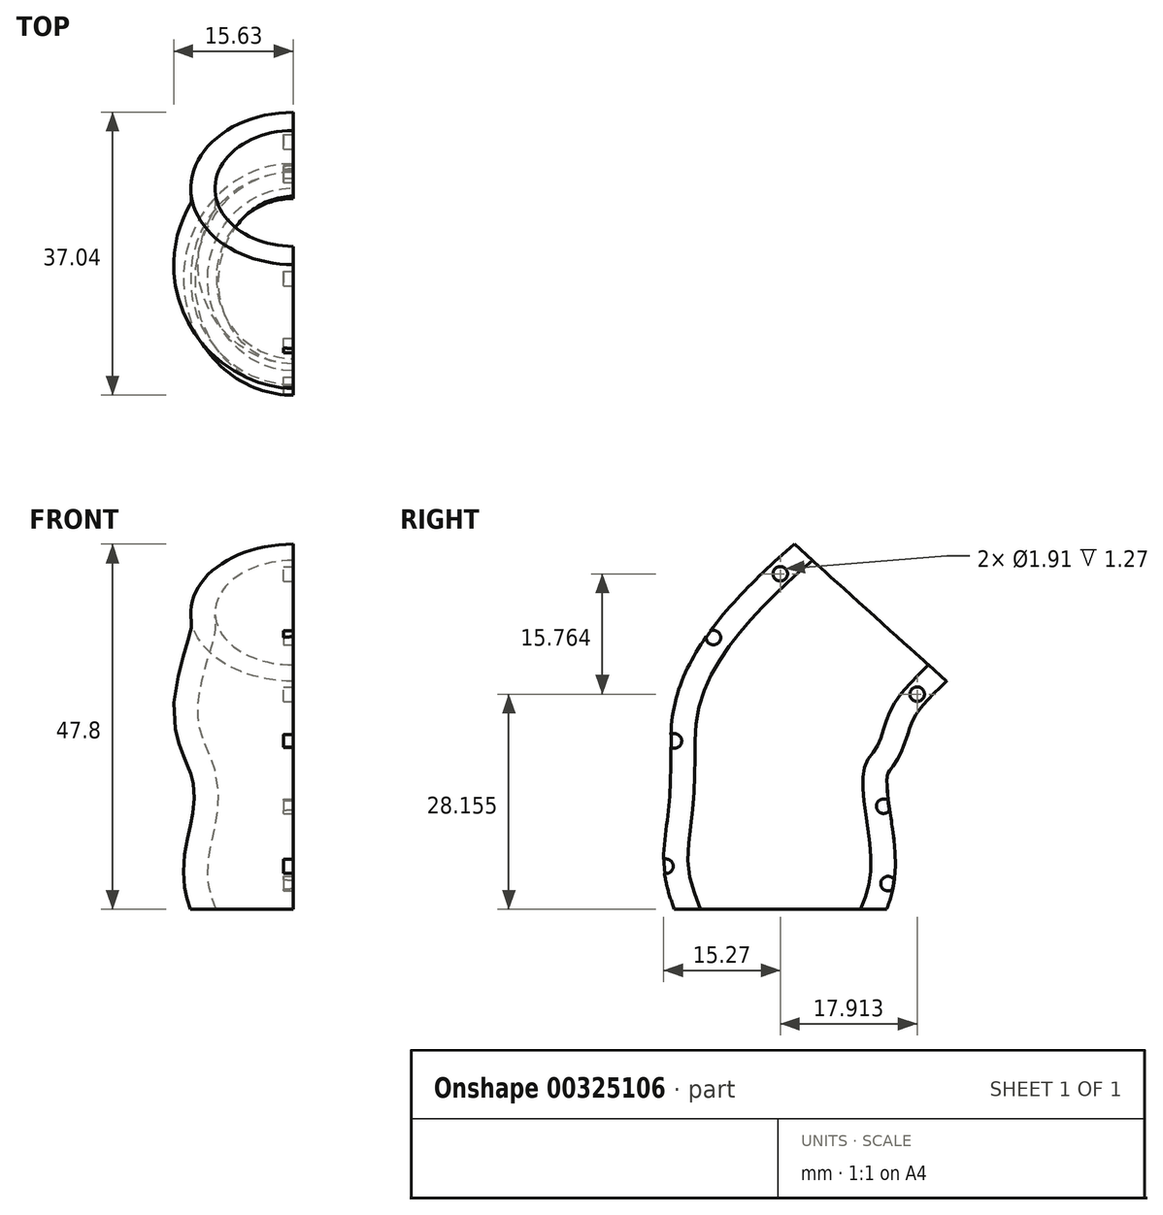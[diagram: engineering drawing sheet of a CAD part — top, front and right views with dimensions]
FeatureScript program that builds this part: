
annotation { "Feature Type Name" : "Feature", "Feature Type Description" : "" }
export const myFeature = defineFeature(function(context is Context, id is Id, definition is map)
    precondition{}
    {
        {
            var Q0;
            Q0=qCreatedBy(makeId("Top.planeOp"),FACE);
            var sketch = newSketch(context, id + "F0", { "sketchPlane" : qUnion([Q0])});
            skEllipse(sketch, "E0", {"center": v(0, 0) * mm, "majorRadius": 10.48 * mm, "minorRadius": 10.06 * mm, "majorAxis": v(0, 1)});
            skSolve(sketch);
        }
        {
            var Q0;
            Q0=qCreatedBy(makeId("Top.planeOp"),FACE);
            cPlane(context, id + "F1", {"entities" : qUnion([Q0]), "cplaneType" : CPlaneType.OFFSET, "offset" : 3.17 * mm, "width" : 152.4 * mm, "height" : 152.4 * mm});
        }
        {
            var Q0;
            Q0=qCreatedBy(id+"F1.planeOp",FACE);
            var sketch = newSketch(context, id + "F2", { "sketchPlane" : qUnion([Q0])});
            skEllipse(sketch, "E1", {"center": v(0, 0) * mm, "majorRadius": 11.6 * mm, "minorRadius": 11.04 * mm, "majorAxis": v(0, 1)});
            skSolve(sketch);
        }
        {
            var Q0;
            Q0=qCreatedBy(makeId("Top.planeOp"),FACE);
            cPlane(context, id + "F3", {"entities" : qUnion([Q0]), "cplaneType" : CPlaneType.OFFSET, "offset" : 19.05 * mm, "width" : 152.4 * mm, "height" : 152.4 * mm});
        }
        {
            var Q0;
            Q0=qCreatedBy(id+"F3.planeOp",FACE);
            var sketch = newSketch(context, id + "F4", { "sketchPlane" : qUnion([Q0])});
            skEllipse(sketch, "E2", {"center": v(0, 0) * mm, "majorRadius": 11.18 * mm, "minorRadius": 10.48 * mm, "majorAxis": v(0, -1)});
            skSolve(sketch);
        }
        {
            var Q0;
            Q0=qCreatedBy(makeId("Right.planeOp"),FACE);
            var sketch = newSketch(context, id + "F5", { "sketchPlane" : qUnion([Q0])});
            skLineSegment(sketch, "E3", {"start": v(-8.35, 25.4) * mm, "end": v(9.56, 21.59) * mm});
            skSolve(sketch);
        }
        {
            var Q0;
            Q0=qCreatedBy(makeId("Right.planeOp"),FACE);
            var Q1;
            Q1=qBodyType(qCreatedBy(id+"F5",EDGE),BodyType.WIRE);
            cPlane(context, id + "F6", {"entities" : qUnion([Q0, Q1]), "cplaneType" : CPlaneType.LINE_ANGLE, "offset" : 25.4 * mm, "angle" : 90 * degree, "width" : 152.4 * mm, "height" : 152.4 * mm});
        }
        {
            var Q0;
            Q0=qCreatedBy(id+"F6.planeOp",FACE);
            var sketch = newSketch(context, id + "F7", { "sketchPlane" : qUnion([Q0])});
            skEllipse(sketch, "E4", {"center": v(0, -4.06) * mm, "majorRadius": 11.87 * mm, "minorRadius": 12.15 * mm, "majorAxis": v(0, 1)});
            skSolve(sketch);
        }
        {
            var Q0;
            Q0=qCreatedBy(id+"F6.planeOp",FACE);
            var sketch = newSketch(context, id + "F8", { "sketchPlane" : qUnion([Q0])});
            skLineSegment(sketch, "E5", {"start": v(11.1, -4.63) * mm, "end": v(-10.76, -4.63) * mm});
            skSolve(sketch);
        }
        {
            var Q0;
            Q0=sQuery(id+"F8.wireOp",EDGE,"E5");
            var Q1;
            Q1=qCreatedBy(id+"F6.planeOp",FACE);
            cPlane(context, id + "F9", {"entities" : qUnion([Q0, Q1]), "cplaneType" : CPlaneType.LINE_ANGLE, "offset" : 25.4 * mm, "angle" : 30 * degree, "width" : 152.4 * mm, "height" : 152.4 * mm});
        }
        {
            var Q0;
            Q0=qCreatedBy(id+"F9.planeOp",FACE);
            cPlane(context, id + "F10", {"entities" : qUnion([Q0]), "cplaneType" : CPlaneType.OFFSET, "offset" : 12.7 * mm, "oppositeDirection" : true, "width" : 152.4 * mm, "height" : 152.4 * mm});
        }
        {
            var Q0;
            Q0=qCreatedBy(id+"F10.planeOp",FACE);
            var sketch = newSketch(context, id + "F11", { "sketchPlane" : qUnion([Q0])});
            skCircle(sketch, "E6", {"center": v(0, 17.54) * mm, "radius": 10.52 * mm});
            skSolve(sketch);
        }
        {
            var Q0;
            Q0=qCreatedBy(id+"F9.planeOp",FACE);
            cPlane(context, id + "F12", {"entities" : qUnion([Q0]), "cplaneType" : CPlaneType.OFFSET, "offset" : 19.05 * mm, "oppositeDirection" : true, "width" : 152.4 * mm, "height" : 152.4 * mm});
        }
        {
            var Q0;
            Q0=qCreatedBy(id+"F12.planeOp",FACE);
            var sketch = newSketch(context, id + "F13", { "sketchPlane" : qUnion([Q0])});
            skCircle(sketch, "E7", {"center": v(0, 17.21) * mm, "radius": 10.21 * mm});
            skSolve(sketch);
        }
        {
            var Q0;
            Q0=qSketchRegion(id+"F0",true);
            var Q1;
            Q1=qSketchRegion(id+"F2",true);
            var Q2;
            Q2=qSketchRegion(id+"F4",true);
            var Q3;
            Q3=makeQuery(id+"F7.imprint","IMPRINT",FACE,{"disambiguationData":[TD([[makeQuery(id+"F7.imprint","IMPRINT",EDGE,{"derivedFrom":sQuery(id+"F7.wireOp",EDGE,"E4")}),1.0]])]});
            var Q4;
            Q4=qSketchRegion(id+"F11",true);
            var Q5;
            Q5=qSketchRegion(id+"F13",true);
            loft(context, id + "F14", {"sheetProfilesArray" : [{ "sheetProfileEntities" : qUnion([Q0]) }, { "sheetProfileEntities" : qUnion([Q1]) }, { "sheetProfileEntities" : qUnion([Q2]) }, { "sheetProfileEntities" : qUnion([Q3]) }, { "sheetProfileEntities" : qUnion([Q4]) }, { "sheetProfileEntities" : qUnion([Q5]) }]});
        }
        {
            var Q0;
            Q0=makeQuery(id+"F14.opLoft","CAP_FACE",FACE,{"disambiguationData":[OSD([makeQuery(id+"F13.imprint","IMPRINT",FACE,{"disambiguationData":[TD([[makeQuery(id+"F13.imprint","IMPRINT",EDGE,{"derivedFrom":sQuery(id+"F13.wireOp",EDGE,"E7")}),1.0]])]})])],"isStart":true});
            var Q1;
            Q1=makeQuery(id+"F14.opLoft","CAP_FACE",FACE,{"disambiguationData":[OSD([makeQuery(id+"F0.imprint","IMPRINT",FACE,{"disambiguationData":[TD([[makeQuery(id+"F0.imprint","IMPRINT",EDGE,{"derivedFrom":sQuery(id+"F0.wireOp",EDGE,"E0")}),1.0]])]})])],"isStart":true});
            var Q2;
            Q2=makeQuery(id+"F14.opLoft","SWEPT_BODY",BODY,{"disambiguationData":[OSD([makeQuery(id+"F0.imprint","IMPRINT",FACE,{"disambiguationData":[TD([[makeQuery(id+"F0.imprint","IMPRINT",EDGE,{"derivedFrom":sQuery(id+"F0.wireOp",EDGE,"E0")}),1.0]])]}),sQuery(id+"F2.wireOp",EDGE,"E1"),sQuery(id+"F4.wireOp",EDGE,"E2"),sQuery(id+"F7.wireOp",EDGE,"E4"),sQuery(id+"F11.wireOp",EDGE,"E6"),makeQuery(id+"F13.imprint","IMPRINT",FACE,{"disambiguationData":[TD([[makeQuery(id+"F13.imprint","IMPRINT",EDGE,{"derivedFrom":sQuery(id+"F13.wireOp",EDGE,"E7")}),1.0]])]})])]});
            shell(context, id + "F15", {"entities" : qUnion([Q0, Q1]), "parts" : qUnion([Q2]), "thickness" : 3.17 * mm, "oppositeDirection" : true});
        }
        {
            var Q0;
            Q0=makeQuery(id+"F14.opLoft","SWEPT_BODY",BODY,{"disambiguationData":[OSD([makeQuery(id+"F0.imprint","IMPRINT",FACE,{"disambiguationData":[TD([[makeQuery(id+"F0.imprint","IMPRINT",EDGE,{"derivedFrom":sQuery(id+"F0.wireOp",EDGE,"E0")}),1.0]])]}),sQuery(id+"F2.wireOp",EDGE,"E1"),sQuery(id+"F4.wireOp",EDGE,"E2"),sQuery(id+"F7.wireOp",EDGE,"E4"),sQuery(id+"F11.wireOp",EDGE,"E6"),makeQuery(id+"F13.imprint","IMPRINT",FACE,{"disambiguationData":[TD([[makeQuery(id+"F13.imprint","IMPRINT",EDGE,{"derivedFrom":sQuery(id+"F13.wireOp",EDGE,"E7")}),1.0]])]})])]});
            transform(context, id + "F16", {"entities" : qUnion([Q0]), "transformType" : TransformType.TRANSLATION_3D, "dx" : 32 * mm, "dy" : 0 * mm, "dz" : 0 * mm, "makeCopy" : true});
        }
        {
            var Q0;
            Q0=makeQuery(id+"F16.opPattern","COPY",BODY,{"derivedFrom":makeQuery(id+"F14.opLoft","SWEPT_BODY",BODY,{"disambiguationData":[OSD([makeQuery(id+"F0.imprint","IMPRINT",FACE,{"disambiguationData":[TD([[makeQuery(id+"F0.imprint","IMPRINT",EDGE,{"derivedFrom":sQuery(id+"F0.wireOp",EDGE,"E0")}),1.0]])]}),sQuery(id+"F2.wireOp",EDGE,"E1"),sQuery(id+"F4.wireOp",EDGE,"E2"),sQuery(id+"F7.wireOp",EDGE,"E4"),sQuery(id+"F11.wireOp",EDGE,"E6"),makeQuery(id+"F13.imprint","IMPRINT",FACE,{"disambiguationData":[TD([[makeQuery(id+"F13.imprint","IMPRINT",EDGE,{"derivedFrom":sQuery(id+"F13.wireOp",EDGE,"E7")}),1.0]])]})])]}),"instanceName":"1"});
            deleteBodies(context, id + "F17", {"entities" : qUnion([Q0])});
        }
        {
            var Q0;
            Q0=qCreatedBy(makeId("Right.planeOp"),FACE);
            var sketch = newSketch(context, id + "F18", { "sketchPlane" : qUnion([Q0])});
            skCircle(sketch, "E8", {"center": v(2.37, 23.36) * mm, "radius": 44.7 * mm});
            skSolve(sketch);
        }
        {
            var Q0;
            Q0=makeQuery(id+"F18.imprint","IMPRINT",FACE,{"disambiguationData":[TD([[makeQuery(id+"F18.imprint","IMPRINT",EDGE,{"derivedFrom":sQuery(id+"F18.wireOp",EDGE,"E8")}),1.0]])]});
            extrude(context, id + "F19", {"entities" : qUnion([Q0]), "operationType" : NewBodyOperationType.REMOVE, "depth" : 50.8 * mm});
        }
        {
            var Q0;
            Q0=qCreatedBy(makeId("Right.planeOp"),FACE);
            var sketch = newSketch(context, id + "F20", { "sketchPlane" : qUnion([Q0])});
            skCircle(sketch, "E9", {"center": v(14.1, 3.36) * mm, "radius": 0.95 * mm});
            skCircle(sketch, "E10", {"center": v(13.53, 13.5) * mm, "radius": 0.95 * mm});
            skCircle(sketch, "E11", {"center": v(17.91, 28.16) * mm, "radius": 0.95 * mm});
            skCircle(sketch, "E12", {"center": v(0, 43.92) * mm, "radius": 0.95 * mm});
            skCircle(sketch, "E13", {"center": v(-8.75, 35.57) * mm, "radius": 0.95 * mm});
            skCircle(sketch, "E14", {"center": v(-13.85, 22.04) * mm, "radius": 0.95 * mm});
            skCircle(sketch, "E15", {"center": v(-14.96, 5.63) * mm, "radius": 0.95 * mm});
            skSolve(sketch);
        }
        {
            var Q0;
            Q0=qSketchRegion(id+"F20",true);
            extrude(context, id + "F21", {"entities" : qUnion([Q0]), "operationType" : NewBodyOperationType.REMOVE, "oppositeDirection" : true, "depth" : 1.27 * mm});
        }
    });
